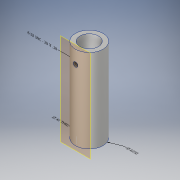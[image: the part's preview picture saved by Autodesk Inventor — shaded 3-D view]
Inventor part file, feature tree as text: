
AUTODESK INVENTOR PART (.ipt)
format: ipt  version: 2018.3 (Build 223284000, 284)  size: 128,000 bytes
history: native  units: in
note: dims shown in document units (in); Inventor stores cm internally (conversion verified against a paired STEP export)
features: hole x4, other x2, sketch x2, extrude x1, plane x1
ambient origin geometry x8: Origin, YZ Plane, XZ Plane, XY Plane, X Axis, Y Axis, Z Axis, Center Point
bodies: Solid1 (feature_tree)
feature tree (10):
  other  "Annotations"
  extrude  "Extrusion1"  Depth=1.0in
  hole  "Hole1"  [1 undecoded]
  plane  "Work Plane1"
  hole  "Hole2"  [1 undecoded]
  sketch  "Sketch1"  dims[d0=1.9in d1=0.0in d38=1.0in d39=1.0in]
  sketch  "Sketch2"  dims[d5=0.5in d6=0.119in d7=0.25in d8=0.5635in d9=1.9in d10=0.8108in d11=1.6in d12=0.104in d13=0.276in d14=0.375in d15=0.25in d16=0.5635in d17=0.3in d18=0.8108in d23=0.0in d25=2.4591in d26=0.3358in d27=0.3804in d29=2.3209in d30=0.625in]
  hole  "Hole Note 1"  [1 undecoded]
  hole  "Hole Note 2"  [1 undecoded]
  other  "Diameter Dimension 1"
note: 4 required parameter values undecoded (feature->parameter linkage not recoverable at this tier; creation-order binding heuristic only, values carry confidence <= 0.55)
